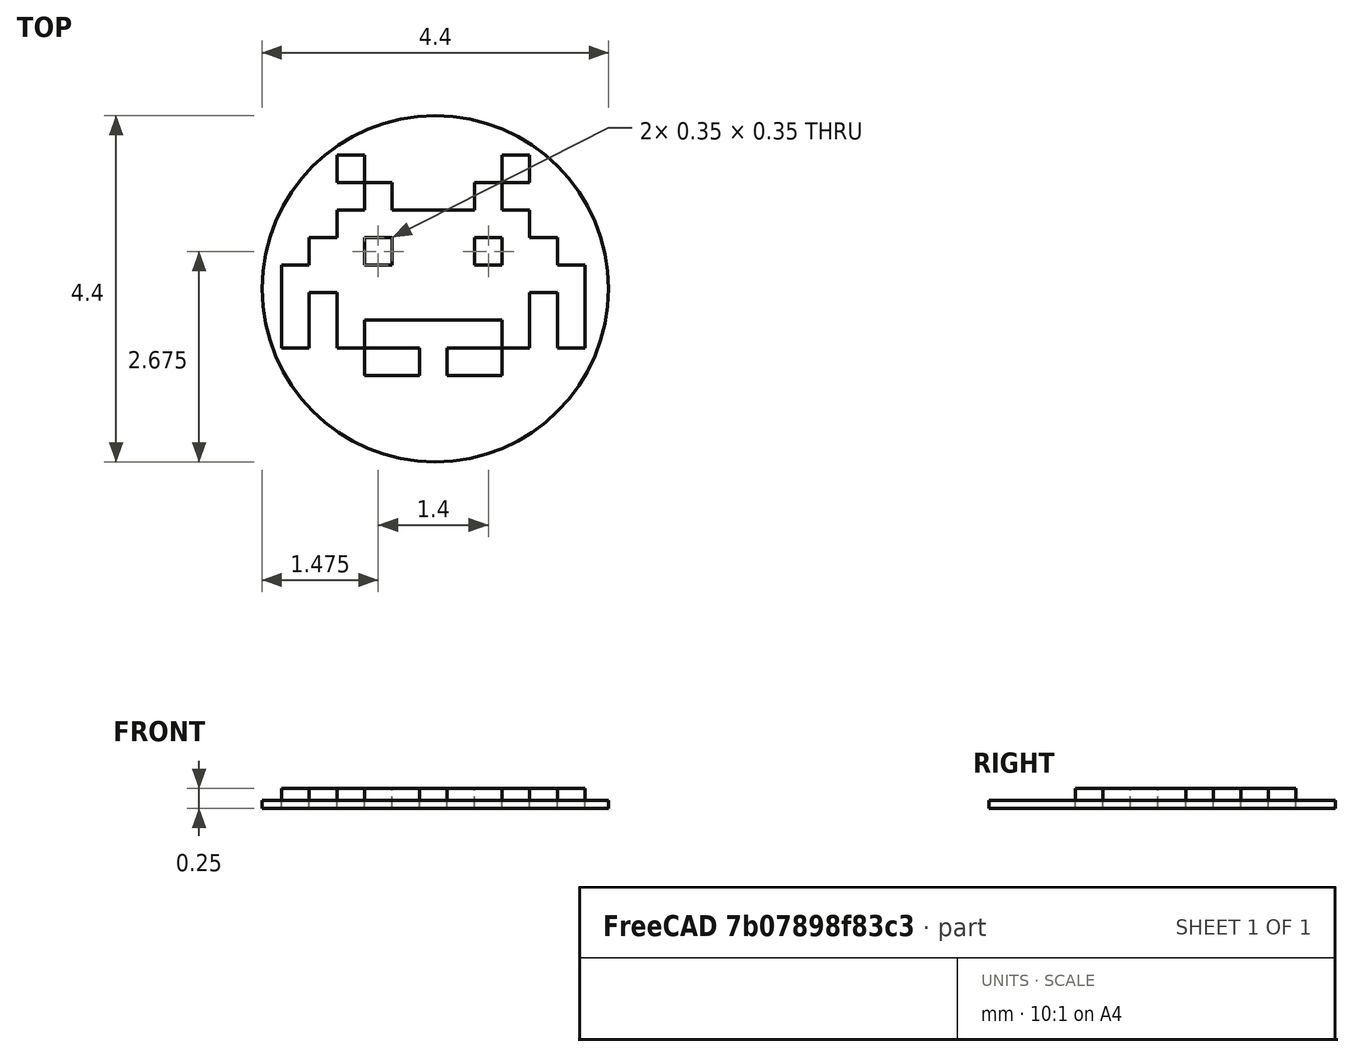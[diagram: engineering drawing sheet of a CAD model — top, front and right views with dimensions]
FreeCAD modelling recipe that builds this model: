
FCSTD DOCUMENT  (FreeCAD 1.0R38806 (Git))
Label: marcianito_space_invaders
License: All rights reserved
LicenseURL: https://en.wikipedia.org/wiki/All_rights_reserved
objects: Part::Box×14, Part::Cut×5, Part::MultiFuse×2, Part::Cylinder×1, Part::Mirroring×1
note: 23 computed .brp shape members not serialized (recipe doc carries the construction recipe); baked Part::Feature solids carry a one-line shape summary decoded from their .brp

FEATURE [Part::Cylinder] Cylinder
  Angle = 360
  AttacherType = Attacher::AttachEngine3D
  FirstAngle = 0
  Height = 0.1
  Radius = 2.2
  SecondAngle = 0
FEATURE [Part::Box] Box  label="Cube"
  AttacherType = Attacher::AttachEngine3D
  Height = 0.25
  Length = 0.35
  Placement = pos=(-1,1,0) rot=(0,0,1;0rad)
  Width = 0.35
FEATURE [Part::Box] Box001  label="Cube001"
  AttacherType = Attacher::AttachEngine3D
  Height = 1
  Length = 0.35
  Placement = pos=(-0.65,-0.05,0) rot=(0,0,1;0rad)
  Width = 0.35
FEATURE [Part::Box] Box002  label="Cube002"
  AttacherType = Attacher::AttachEngine3D
  Height = 0.25
  Length = 1.05
  Placement = pos=(-1,0.3,0) rot=(0,0,1;0rad)
  Width = 0.35
FEATURE [Part::Box] Box003  label="Cube003"
  AttacherType = Attacher::AttachEngine3D
  Height = 0.25
  Length = 1.4
  Placement = pos=(-1.35,-0.05,0) rot=(0,0,1;0rad)
  Width = 0.35
FEATURE [Part::Box] Box004  label="Cube004"
  AttacherType = Attacher::AttachEngine3D
  Height = 0.25
  Length = 1.75
  Placement = pos=(-1.7,-0.4,0) rot=(0,0,1;0rad)
  Width = 0.35
FEATURE [Part::Box] Box005  label="Cube005"
  AttacherType = Attacher::AttachEngine3D
  Height = 0.25
  Length = 1.75
  Placement = pos=(-1.7,-0.75,0) rot=(0,0,1;0rad)
  Width = 0.35
FEATURE [Part::Box] Box006  label="Cube006"
  AttacherType = Attacher::AttachEngine3D
  Height = 0.25
  Length = 1.75
  Placement = pos=(-1.7,-1.1,0) rot=(0,0,1;0rad)
  Width = 0.35
FEATURE [Part::Box] Box007  label="Cube007"
  AttacherType = Attacher::AttachEngine3D
  Height = 0.25
  Length = 1.75
  Placement = pos=(-1.7,-1.45,0) rot=(0,0,1;0rad)
  Width = 0.35
FEATURE [Part::Box] Box008  label="Cube008"
  AttacherType = Attacher::AttachEngine3D
  Height = 0.25
  Length = 0.35
  Placement = pos=(-0.65,0.65,0) rot=(0,0,1;0rad)
  Width = 0.35
FEATURE [Part::Cut] Cut
  Base = -> Box003
  Refine = true
  Tool = -> Box001
FEATURE [Part::Box] Box009  label="Cube009"
  AttacherType = Attacher::AttachEngine3D
  Height = 1
  Length = 0.35
  Placement = pos=(-1.35,-1.1,0) rot=(0,0,1;0rad)
  Width = 0.7
FEATURE [Part::Box] Box010  label="Cube010"
  AttacherType = Attacher::AttachEngine3D
  Height = 1
  Length = 1.05
  Placement = pos=(-1.7,-1.45,0) rot=(0,0,1;0rad)
  Width = 0.35
FEATURE [Part::Cut] Cut001
  Base = -> Box007
  Refine = true
  Tool = -> Box010
FEATURE [Part::Box] Box011  label="Cube011"
  AttacherType = Attacher::AttachEngine3D
  Height = 1
  Length = 1.75
  Placement = pos=(-1.7,-1.45,0) rot=(0,0,1;0rad)
  Width = 0.35
FEATURE [Part::Box] Box012  label="Cube012"
  AttacherType = Attacher::AttachEngine3D
  Height = 1
  Length = 1.05
  Placement = pos=(-1.7,-1.45,0) rot=(0,0,1;0rad)
  Width = 0.35
FEATURE [Part::Cut] Cut002
  Base = -> Box011
  Placement = pos=(0,0.35,0) rot=(0,0,1;0rad)
  Refine = true
  Tool = -> Box012
FEATURE [Part::Cut] Cut003
  Base = -> Box006
  Refine = true
  Tool = -> Cut002
FEATURE [Part::Box] Box013  label="Cube013"
  AttacherType = Attacher::AttachEngine3D
  Height = 0.25
  Length = 1.4
  Placement = pos=(0.4,-0.75,0) rot=(0,0,1;1.5708rad)
  Width = 0.35
FEATURE [Part::MultiFuse] Fusion
  Refine = true
  Shapes = -> [Cut003,Cut001,Cut,Box008,Box005,Box004,Box002,Box]
FEATURE [Part::Cut] Cut004  label="left_side"
  Base = -> Fusion
  Refine = true
  Tool = -> Box009
FEATURE [Part::Mirroring] Mirror  label="left_side (mirrored)"
  Base = (0.05,0.65,0)
  Normal = (-1,0,0)
  Placement = pos=(0.35,0,0) rot=(0,0,1;0rad)
  Source = -> Cut004
FEATURE [Part::MultiFuse] Fusion001
  Placement = pos=(-0.25,0.35,0) rot=(0,0,1;0rad)
  Refine = true
  Shapes = -> [Cut004,Mirror,Box013]
